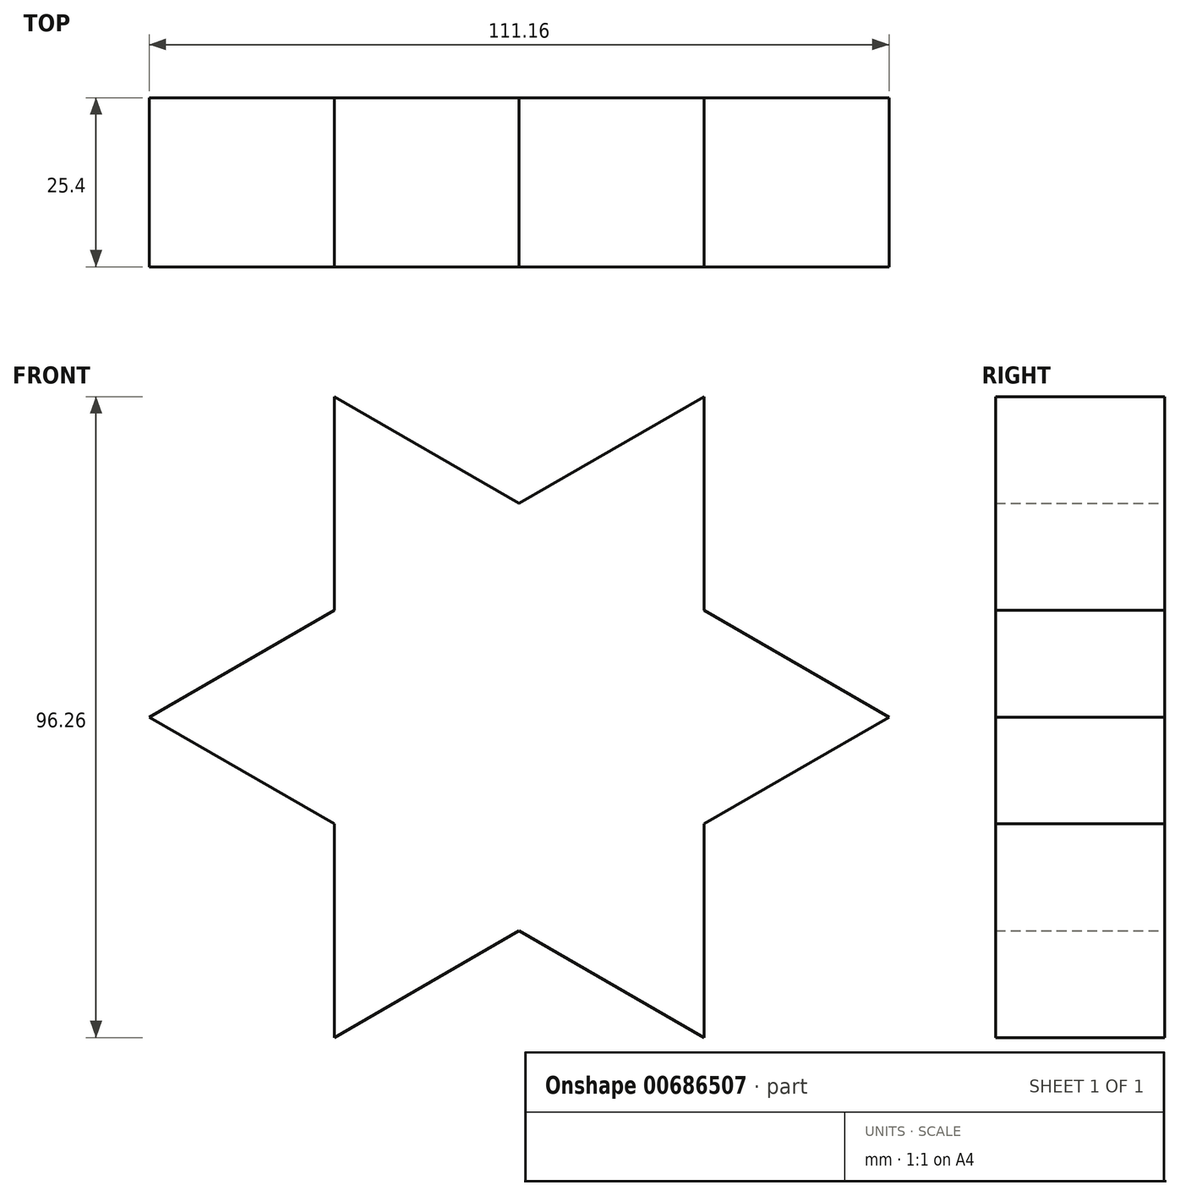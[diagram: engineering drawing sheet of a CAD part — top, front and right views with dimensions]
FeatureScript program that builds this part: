
annotation { "Feature Type Name" : "Feature", "Feature Type Description" : "" }
export const myFeature = defineFeature(function(context is Context, id is Id, definition is map)
    precondition{}
    {
        {
            var Q0;
            Q0=qCreatedBy(makeId("Front.planeOp"),FACE);
            var sketch = newSketch(context, id + "F0", { "sketchPlane" : qUnion([Q0])});
            skLineSegment(sketch, "E0.0", {"start": v(0, 32.09) * mm, "end": v(27.79, 16.04) * mm});
            skLineSegment(sketch, "E0.1", {"start": v(27.79, 16.04) * mm, "end": v(27.79, -16.04) * mm});
            skLineSegment(sketch, "E0.2", {"start": v(27.79, -16.04) * mm, "end": v(0, -32.09) * mm});
            skLineSegment(sketch, "E0.3", {"start": v(0, -32.09) * mm, "end": v(-27.79, -16.04) * mm});
            skLineSegment(sketch, "E0.4", {"start": v(-27.79, -16.04) * mm, "end": v(-27.79, 16.04) * mm});
            skLineSegment(sketch, "E0.5", {"start": v(-27.79, 16.04) * mm, "end": v(0, 32.09) * mm});
            skLineSegment(sketch, "E1", {"start": v(-27.79, 16.04) * mm, "end": v(-27.79, 48.13) * mm});
            skLineSegment(sketch, "E2", {"start": v(-27.79, 48.13) * mm, "end": v(0, 32.09) * mm});
            skLineSegment(sketch, "E3", {"start": v(0, 32.09) * mm, "end": v(27.79, 48.13) * mm});
            skLineSegment(sketch, "E4", {"start": v(27.79, 48.13) * mm, "end": v(27.79, 16.04) * mm});
            skLineSegment(sketch, "E5", {"start": v(27.79, 16.04) * mm, "end": v(55.58, 0) * mm});
            skLineSegment(sketch, "E6", {"start": v(55.58, 0) * mm, "end": v(27.79, -16.04) * mm});
            skLineSegment(sketch, "E7", {"start": v(27.79, -16.04) * mm, "end": v(27.79, -48.13) * mm});
            skLineSegment(sketch, "E8", {"start": v(27.79, -48.13) * mm, "end": v(0, -32.09) * mm});
            skLineSegment(sketch, "E9", {"start": v(0, -32.09) * mm, "end": v(-27.79, -48.13) * mm});
            skLineSegment(sketch, "E10", {"start": v(-27.79, -48.13) * mm, "end": v(-27.79, -16.04) * mm});
            skLineSegment(sketch, "E11", {"start": v(-27.79, -16.04) * mm, "end": v(-55.58, 0) * mm});
            skLineSegment(sketch, "E12", {"start": v(-55.58, 0) * mm, "end": v(-27.79, 16.04) * mm});
            skSolve(sketch);
        }
        {
            var Q0;
            Q0 = qSketchRegion(id + "F0", true);
            extrude(context, id + "F1", {"entities" : qUnion([Q0]), "depth" : 25.4 * mm, "offsetDistance" : 25.4 * mm});
        }
    });
